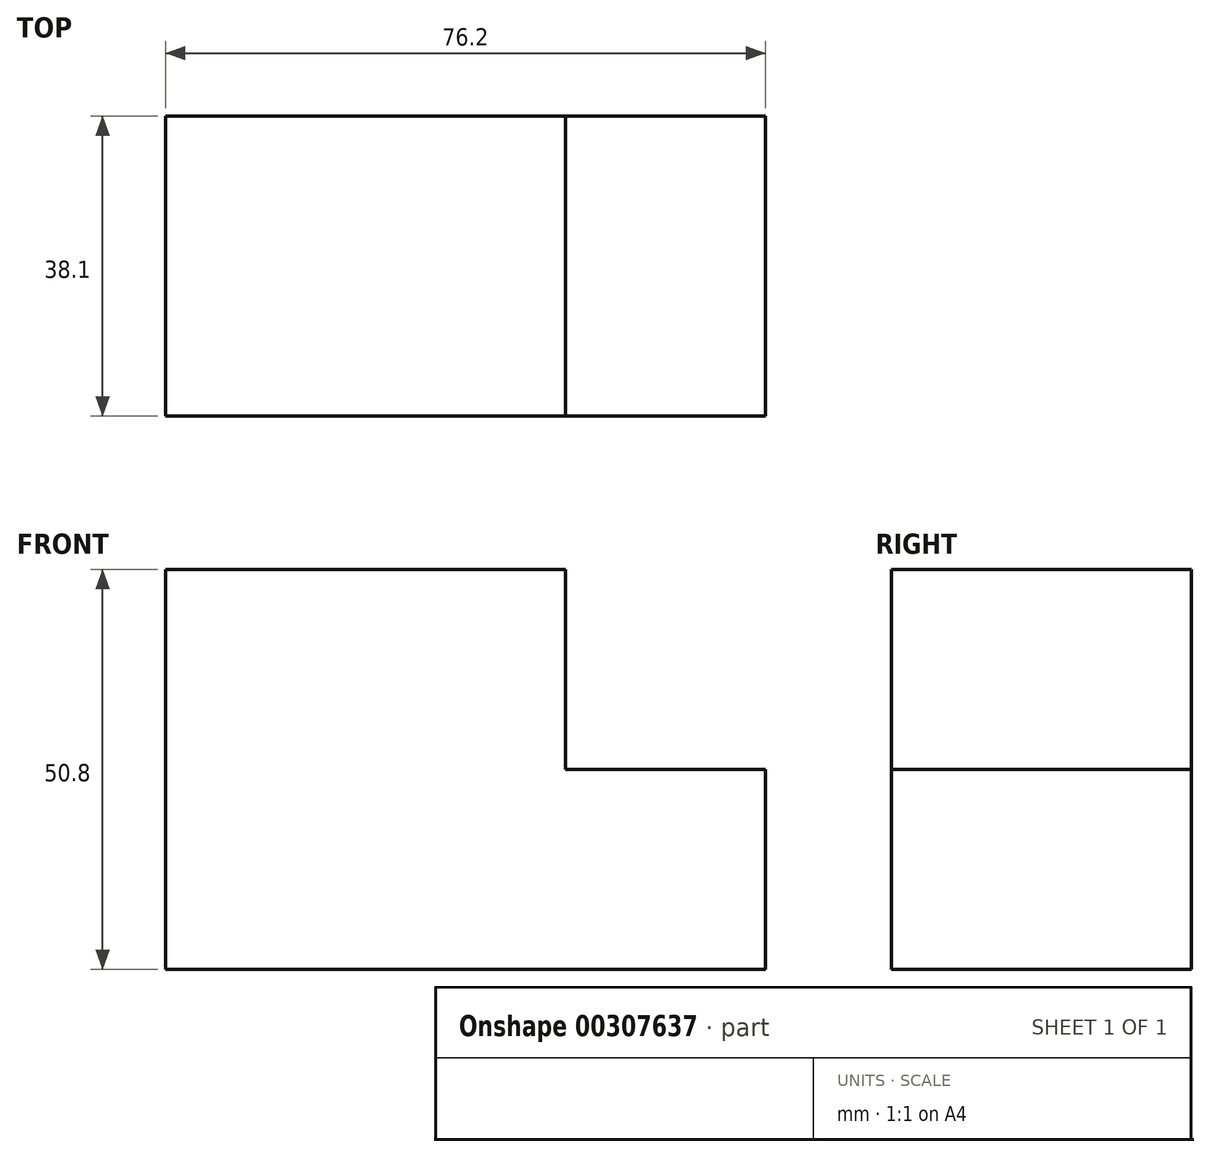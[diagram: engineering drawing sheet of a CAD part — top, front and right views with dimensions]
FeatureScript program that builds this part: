
annotation { "Feature Type Name" : "Feature", "Feature Type Description" : "" }
export const myFeature = defineFeature(function(context is Context, id is Id, definition is map)
    precondition{}
    {
        {
            var Q0;
            Q0=qCreatedBy(makeId("Front.planeOp"),FACE);
            var sketch = newSketch(context, id + "F0", { "sketchPlane" : qUnion([Q0])});
            skLineSegment(sketch, "E0", {"start": v(-50.8, -35.81) * mm, "end": v(25.4, -35.81) * mm});
            skLineSegment(sketch, "E1", {"start": v(25.4, -35.81) * mm, "end": v(25.4, -10.41) * mm});
            skLineSegment(sketch, "E2", {"start": v(25.4, -10.41) * mm, "end": v(0, -10.41) * mm});
            skLineSegment(sketch, "E3", {"start": v(0, -10.41) * mm, "end": v(0, 14.99) * mm});
            skLineSegment(sketch, "E4", {"start": v(0, 14.99) * mm, "end": v(-50.8, 14.99) * mm});
            skLineSegment(sketch, "E5", {"start": v(-50.8, 14.99) * mm, "end": v(-50.8, -35.81) * mm});
            skSolve(sketch);
        }
        {
            var Q0;
            Q0=makeQuery(id+"F0.imprint","IMPRINT",FACE,{"disambiguationData":[TD([[makeQuery(id+"F0.imprint","IMPRINT",EDGE,{"derivedFrom":sQuery(id+"F0.wireOp",EDGE,"E0")}),1.0]])]});
            extrude(context, id + "F1", {"entities" : qUnion([Q0]), "depth" : 38.1 * mm});
        }
    });
